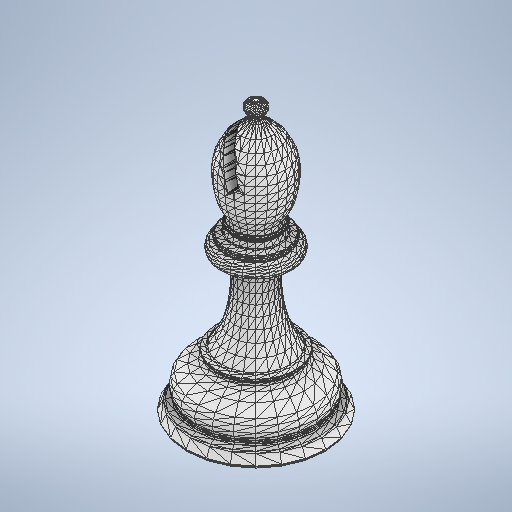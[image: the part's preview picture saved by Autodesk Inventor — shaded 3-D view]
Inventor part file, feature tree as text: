
AUTODESK INVENTOR PART (.ipt)
format: ipt  version: 2025.2 (Build 292293000, 293)  size: 6,794,752 bytes
history: native  units: mm
features: other x4, move_body x3, direct_edit x1, extrude x1, chamfer x1, sketch x1
ambient origin geometry x8: Origin, YZ Plane, XZ Plane, XY Plane, X Axis, Y Axis, Z Axis, Center Point
bodies: Body1 (feature_tree)
feature tree (11):
  other  "ChessSet v2.ipt"
  other  "Work Axis1"
  move_body  "Move Body1"
  direct_edit  "Direct Edit1"
  move_body  "Move Body2"
  extrude  "Extrusion1"  TaperAngle=90.0deg  [1 undecoded]
  chamfer  "Chamfer1"  [1 undecoded]
  other  "Solid3::ChessSet v2.ipt"
  other  "TaggingFeature1"
  sketch  "Sketch1"  dims[d0=10.0mm d1=90.0deg d2=-123.902544mm d3=0.0mm d4=-5.36425mm d5=-8.911mm d6=0.0mm d7=0.0mm d8=10.2mm d9=2.2mm d10=0.0mm d11=0.5mm d12=2.0mm d13=45.0deg]
  move_body  "Move1"
note: 2 required parameter values undecoded (feature->parameter linkage not recoverable at this tier; creation-order binding heuristic only, values carry confidence <= 0.55)
